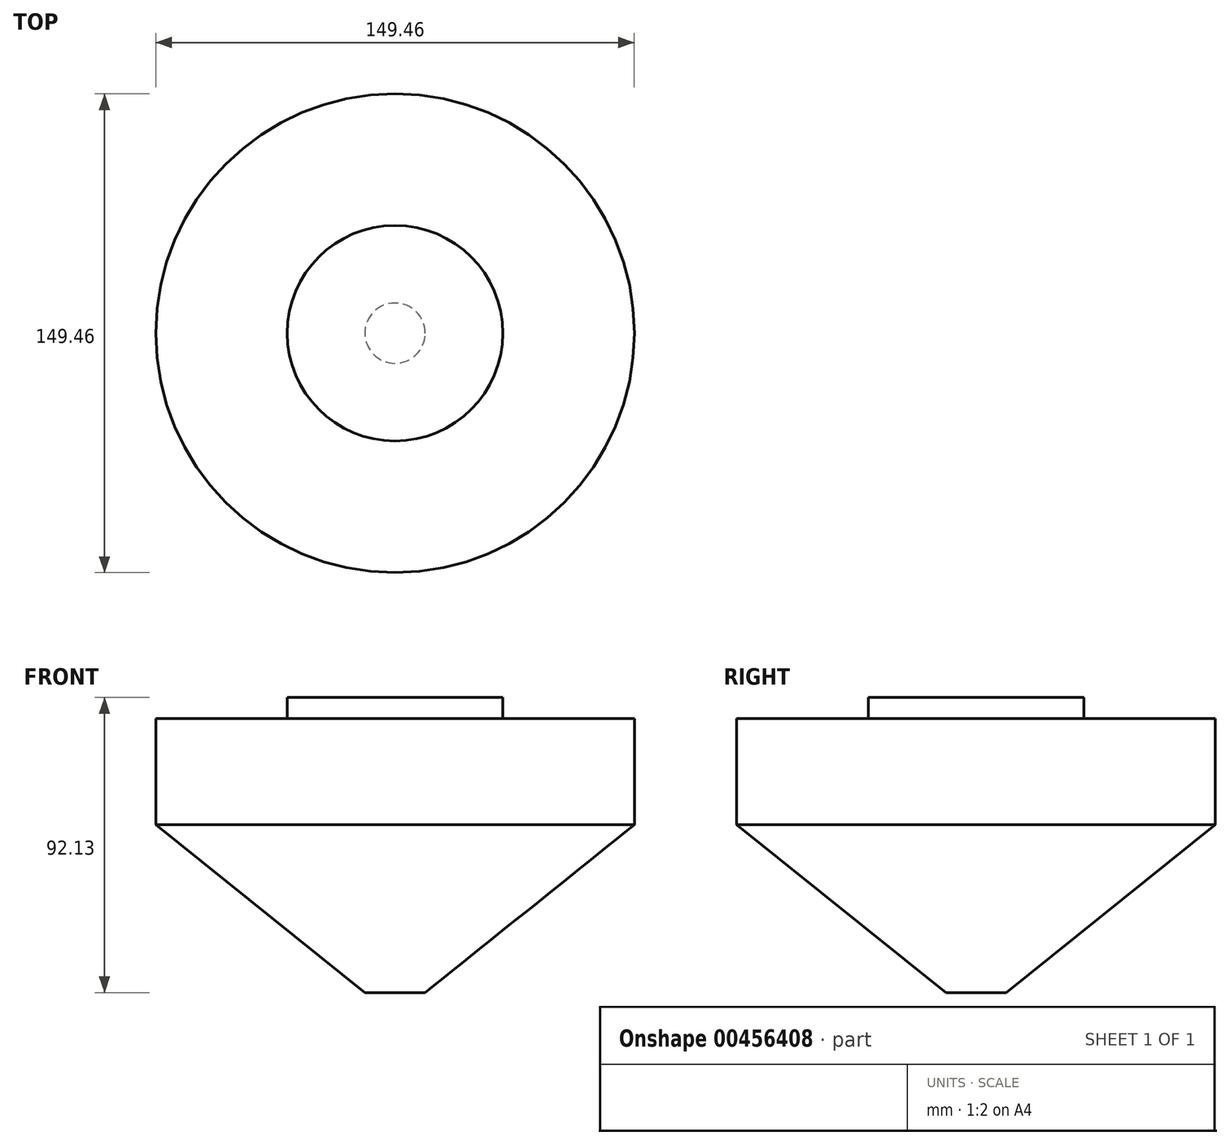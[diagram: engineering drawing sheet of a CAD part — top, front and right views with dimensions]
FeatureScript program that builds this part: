
annotation { "Feature Type Name" : "Feature", "Feature Type Description" : "" }
export const myFeature = defineFeature(function(context is Context, id is Id, definition is map)
    precondition{}
    {
        {
            var Q0;
            Q0=qCreatedBy(makeId("Front.planeOp"),FACE);
            var sketch = newSketch(context, id + "F0", { "sketchPlane" : qUnion([Q0])});
            skLineSegment(sketch, "E0", {"start": v(0, 39.8) * mm, "end": v(33.66, 39.8) * mm});
            skLineSegment(sketch, "E1", {"start": v(33.66, 39.8) * mm, "end": v(33.66, 33.23) * mm});
            skLineSegment(sketch, "E2", {"start": v(33.66, 33.23) * mm, "end": v(74.73, 33.23) * mm});
            skLineSegment(sketch, "E3", {"start": v(74.73, 33.23) * mm, "end": v(74.73, 0) * mm});
            skLineSegment(sketch, "E4", {"start": v(74.73, 0) * mm, "end": v(9.41, -52.34) * mm});
            skLineSegment(sketch, "E5", {"start": v(9.41, -52.34) * mm, "end": v(0, -52.34) * mm});
            skLineSegment(sketch, "E6", {"start": v(0, 39.8) * mm, "end": v(0, 0) * mm});
            skLineSegment(sketch, "E7", {"start": v(0, 0) * mm, "end": v(0, -52.34) * mm});
            skSolve(sketch);
        }
        {
            var Q0;
            Q0=makeQuery(id+"F0.imprint","IMPRINT",FACE,{"disambiguationData":[TD([[makeQuery(id+"F0.imprint","IMPRINT",EDGE,{"derivedFrom":sQuery(id+"F0.wireOp",EDGE,"E0")}),-1.0]])]});
            var Q1;
            Q1=sQuery(id+"F0.wireOp",EDGE,"E7");
            revolve(context, id + "F1", {"entities" : qUnion([Q0]), "axis" : qUnion([Q1]), "revolveType" : RevolveType.FULL});
        }
    });
